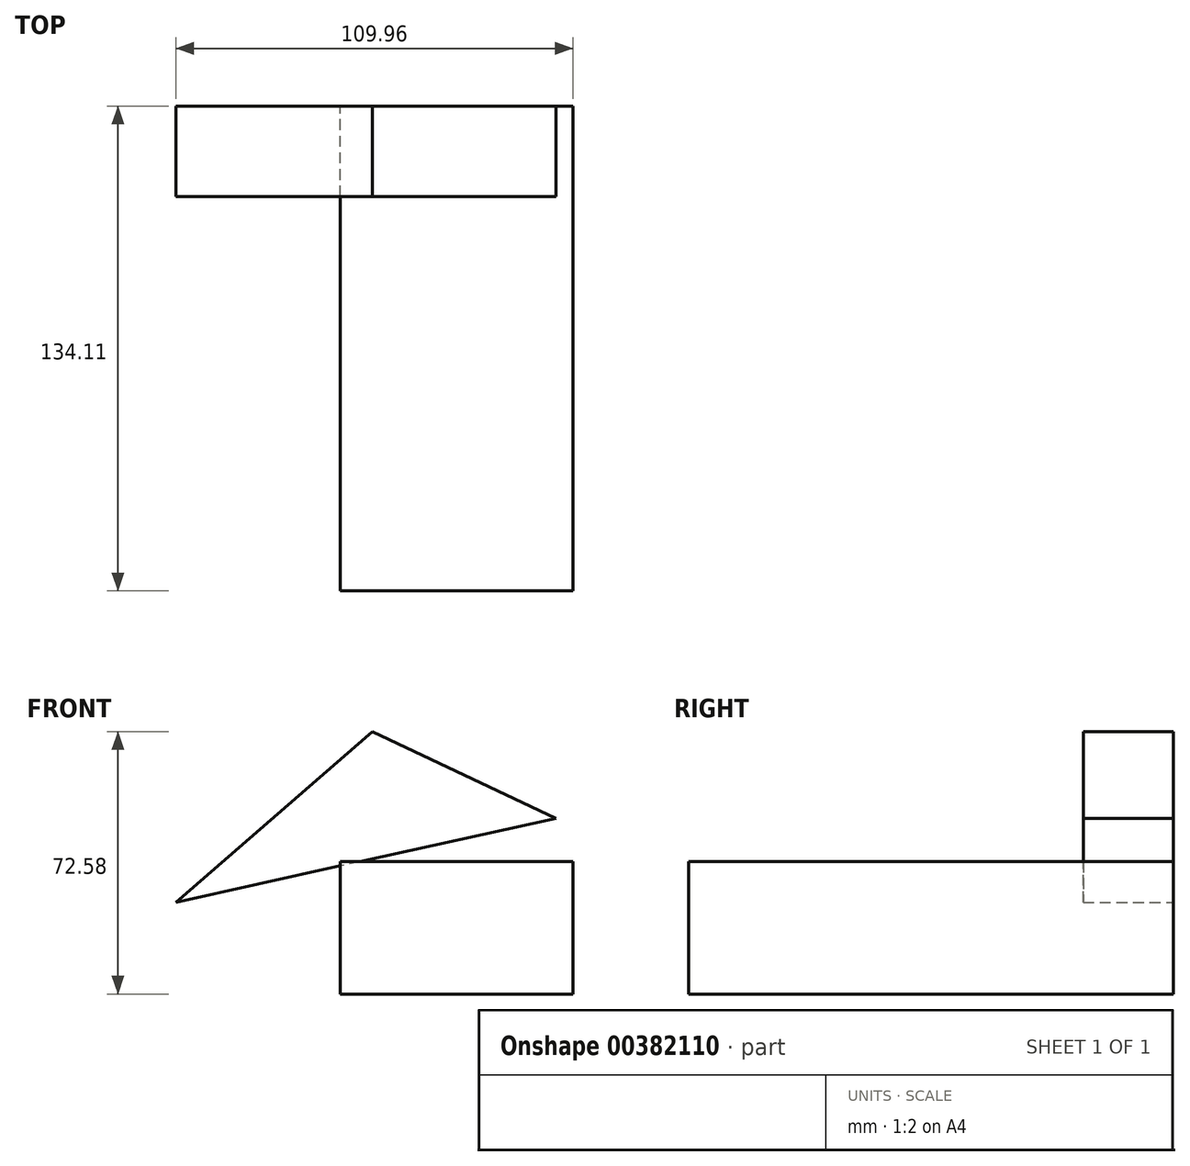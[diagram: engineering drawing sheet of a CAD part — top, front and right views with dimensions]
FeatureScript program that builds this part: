
annotation { "Feature Type Name" : "Feature", "Feature Type Description" : "" }
export const myFeature = defineFeature(function(context is Context, id is Id, definition is map)
    precondition{}
    {
        {
            var Q0;
            Q0=qCreatedBy(makeId("Front.planeOp"),FACE);
            var sketch = newSketch(context, id + "F0", { "sketchPlane" : qUnion([Q0])});
            skLineSegment(sketch, "E0", {"start": v(-45.54, -11.25) * mm, "end": v(8.9, 35.93) * mm});
            skLineSegment(sketch, "E1", {"start": v(8.9, 35.93) * mm, "end": v(59.7, 11.98) * mm});
            skLineSegment(sketch, "E2", {"start": v(59.7, 11.98) * mm, "end": v(-45.54, -11.25) * mm});
            skSolve(sketch);
        }
        {
            var Q0;
            Q0 = qSketchRegion(id + "F0", true);
            extrude(context, id + "F1", {"entities" : qUnion([Q0]), "depth" : 25 * mm});
        }
        {
            var Q0;
            Q0=qCreatedBy(makeId("Front.planeOp"),FACE);
            var sketch = newSketch(context, id + "F2", { "sketchPlane" : qUnion([Q0])});
            skLineSegment(sketch, "E3.bottom", {"start": v(0, 0) * mm, "end": v(64.42, 0) * mm});
            skLineSegment(sketch, "E3.top", {"start": v(0, -36.65) * mm, "end": v(64.42, -36.65) * mm});
            skLineSegment(sketch, "E3.left", {"start": v(0, 0) * mm, "end": v(0, -36.65) * mm});
            skLineSegment(sketch, "E3.right", {"start": v(64.42, 0) * mm, "end": v(64.42, -36.65) * mm});
            skSolve(sketch);
        }
        {
            var Q0;
            Q0 = qSketchRegion(id + "F2", true);
            extrude(context, id + "F3", {"entities" : qUnion([Q0]), "endBound" : BoundingType.THROUGH_ALL, "depth" : 25 * mm});
        }
    });
